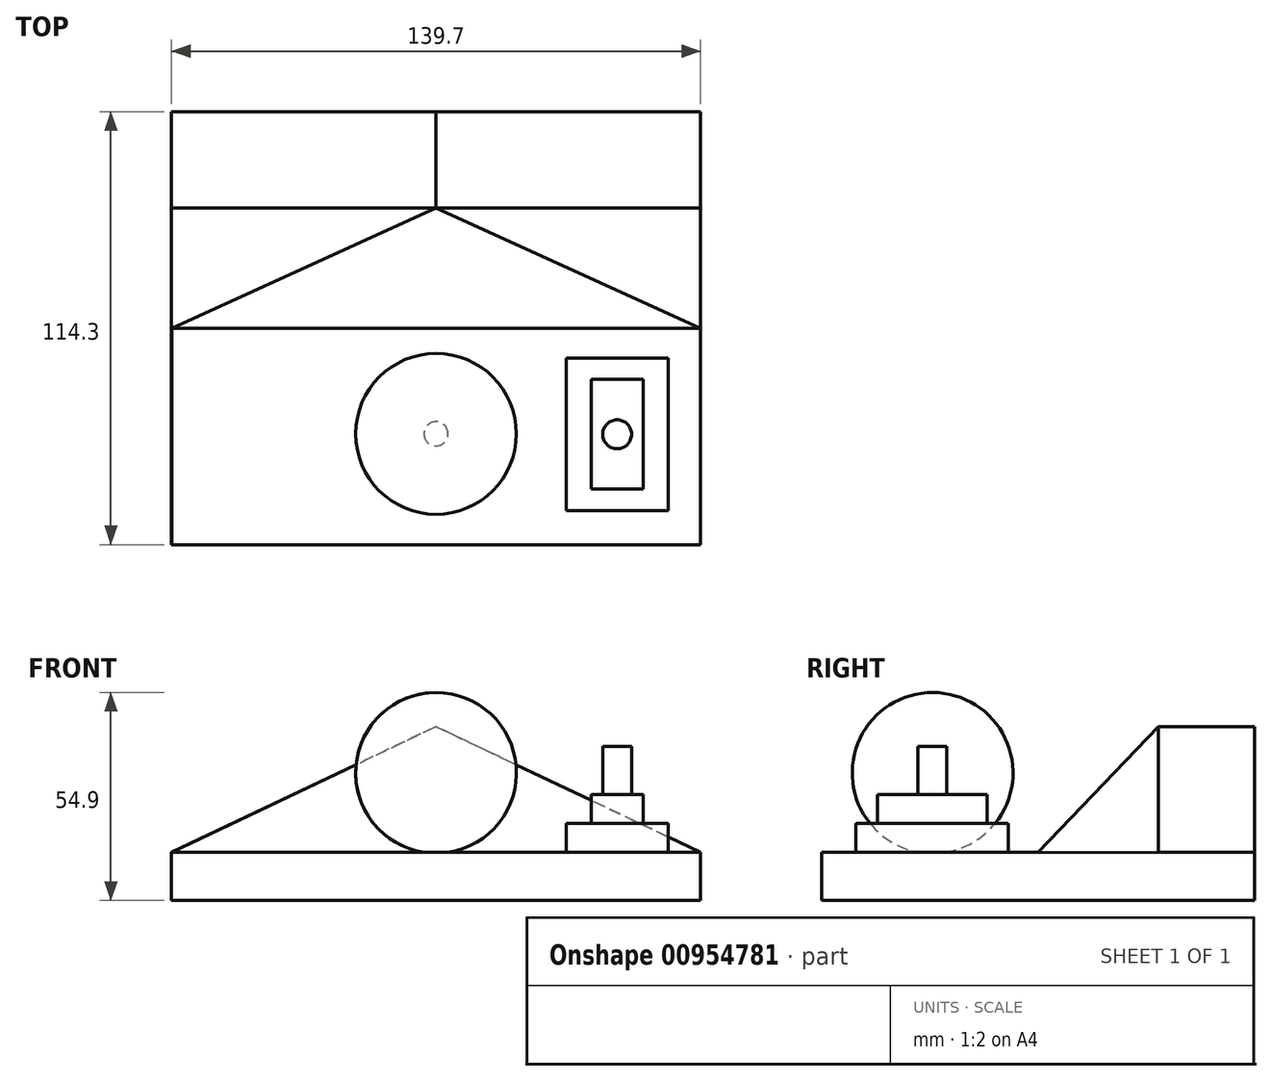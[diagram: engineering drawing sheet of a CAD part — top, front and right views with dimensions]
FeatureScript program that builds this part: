
annotation { "Feature Type Name" : "Feature", "Feature Type Description" : "" }
export const myFeature = defineFeature(function(context is Context, id is Id, definition is map)
    precondition{}
    {
        {
            var Q0;
            Q0=qCreatedBy(makeId("Top.planeOp"),FACE);
            var sketch = newSketch(context, id + "F0", { "sketchPlane" : qUnion([Q0])});
            skLineSegment(sketch, "E0.bottom", {"start": v(69.85, 57.15) * mm, "end": v(-69.85, 57.15) * mm});
            skLineSegment(sketch, "E0.top", {"start": v(69.85, -57.15) * mm, "end": v(-69.85, -57.15) * mm});
            skLineSegment(sketch, "E0.left", {"start": v(69.85, 57.15) * mm, "end": v(69.85, -57.15) * mm});
            skLineSegment(sketch, "E0.right", {"start": v(-69.85, 57.15) * mm, "end": v(-69.85, -57.15) * mm});
            skPoint(sketch, "E0.middle", {"position": v(0, 0) * mm});
            skSolve(sketch);
        }
        {
            var Q0;
            Q0=makeQuery(id+"F0.imprint","IMPRINT",FACE,{"disambiguationData":[TD([[makeQuery(id+"F0.imprint","IMPRINT",EDGE,{"derivedFrom":sQuery(id+"F0.wireOp",EDGE,"E0.bottom")}),1.0]])]});
            extrude(context, id + "F1", {"entities" : qUnion([Q0]), "depth" : 12.7 * mm, "offsetDistance" : 25.4 * mm});
        }
        {
            var Q0;
            Q0=makeQuery(id+"F1.opExtrude","SWEPT_FACE",FACE,{"disambiguationData":[OSD([sQuery(id+"F0.wireOp",EDGE,"E0.bottom")])]});
            var sketch = newSketch(context, id + "F2", { "sketchPlane" : qUnion([Q0])});
            skLineSegment(sketch, "E1", {"start": v(69.85, 12.7) * mm, "end": v(0, 45.9) * mm});
            skLineSegment(sketch, "E2", {"start": v(0, 45.9) * mm, "end": v(-69.85, 12.7) * mm});
            skLineSegment(sketch, "E3", {"start": v(-69.85, 12.7) * mm, "end": v(69.85, 12.7) * mm});
            skSolve(sketch);
        }
        {
            var Q0;
            Q0=makeQuery(id+"F2.imprint","IMPRINT",FACE,{"disambiguationData":[TD([[makeQuery(id+"F2.imprint","IMPRINT",EDGE,{"derivedFrom":sQuery(id+"F2.wireOp",EDGE,"E1")}),1.0]])]});
            extrude(context, id + "F3", {"entities" : qUnion([Q0]), "oppositeDirection" : true, "depth" : 25.4 * mm, "offsetDistance" : 25.4 * mm});
        }
        {
            var Q0;
            Q0=qCreatedBy(makeId("Right.planeOp"),FACE);
            var sketch = newSketch(context, id + "F4", { "sketchPlane" : qUnion([Q0])});
            skLineSegment(sketch, "E4", {"start": v(0, 12.7) * mm, "end": v(31.75, 12.7) * mm});
            skLineSegment(sketch, "E5", {"start": v(31.75, 12.7) * mm, "end": v(31.73, 45.9) * mm});
            skLineSegment(sketch, "E6", {"start": v(31.73, 45.9) * mm, "end": v(0, 12.7) * mm});
            skSolve(sketch);
        }
        {
            var Q0;
            Q0 = qSketchRegion(id + "F4", true);
            extrude(context, id + "F5", {"entities" : qUnion([Q0]), "operationType" : NewBodyOperationType.ADD, "endBound" : BoundingType.SYMMETRIC, "depth" : 139.7 * mm, "offsetDistance" : 25.4 * mm});
        }
        {
            var Q0;
            Q0=makeQuery(id+"F5.opExtrude","SWEPT_FACE",FACE,{"disambiguationData":[OSD([sQuery(id+"F4.wireOp",EDGE,"E5")])]});
            var sketch = newSketch(context, id + "F6", { "sketchPlane" : qUnion([Q0])});
            skLineSegment(sketch, "E7", {"start": v(-69.85, 12.69) * mm, "end": v(0, 45.88) * mm});
            skLineSegment(sketch, "E8", {"start": v(0, 45.88) * mm, "end": v(69.85, 12.69) * mm});
            skLineSegment(sketch, "E9", {"start": v(69.85, 12.69) * mm, "end": v(69.85, 45.88) * mm});
            skLineSegment(sketch, "E10", {"start": v(69.85, 45.88) * mm, "end": v(-69.85, 45.88) * mm});
            skLineSegment(sketch, "E11", {"start": v(-69.85, 45.88) * mm, "end": v(-69.85, 12.69) * mm});
            skSolve(sketch);
        }
        {
            var Q0;
            Q0 = qSketchRegion(id + "F6", true);
            extrude(context, id + "F7", {"entities" : qUnion([Q0]), "operationType" : NewBodyOperationType.REMOVE, "oppositeDirection" : true, "depth" : 152.4 * mm, "offsetDistance" : 25.4 * mm});
        }
        {
            var Q0;
            Q0=qCreatedBy(makeId("Front.planeOp"),FACE);
            cPlane(context, id + "F8", {"entities" : qUnion([Q0]), "cplaneType" : CPlaneType.OFFSET, "offset" : 27.9 * mm, "width" : 152.4 * mm, "height" : 152.4 * mm});
        }
        {
            var Q0;
            Q0=qCreatedBy(id+"F8.planeOp",FACE);
            var sketch = newSketch(context, id + "F9", { "sketchPlane" : qUnion([Q0])});
            skArc(sketch, "E12", {"start": v(0, 12.46) * mm, "mid": v(21.22, 33.68) * mm, "end": v(0, 54.9) * mm});
            skLineSegment(sketch, "E13", {"start": v(0, 54.9) * mm, "end": v(0, 12.46) * mm});
            skSolve(sketch);
        }
        {
            var Q0;
            Q0=qCreatedBy(id+"F8.planeOp",FACE);
            var sketch = newSketch(context, id + "F10", { "sketchPlane" : qUnion([Q0])});
            skLineSegment(sketch, "E14", {"start": v(0, 0) * mm, "end": v(0, 61.95) * mm});
            skSolve(sketch);
        }
        {
            var Q0;
            Q0 = qSketchRegion(id + "F9", true);
            var Q1;
            Q1 = qSketchRegion(id + "F10", true);
            var Q2;
            Q2=sQuery(id+"F10.wireOp",EDGE,"E14");
            var Q3;
            Q3=sQuery(id+"F10.wireOp",EDGE,"E14");
            revolve(context, id + "F11", {"operationType" : NewBodyOperationType.ADD, "surfaceOperationType" : NewSurfaceOperationType.NEW, "entities" : qUnion([Q0, Q1]), "axis" : qUnion([Q2, Q3]), "revolveType" : RevolveType.FULL});
        }
        {
            var Q0;
            {var subQ3=sQuery(id+"F0.wireOp",EDGE,"E0.top");var subQ4=sQuery(id+"F0.wireOp",EDGE,"E0.right");var subQ5=sQuery(id+"F0.wireOp",EDGE,"E0.left");Q0=makeQuery(id+"F5.boolean.opBoolean","SPLIT",FACE,{"disambiguationData":[TD([makeQuery(id+"F1.opExtrude","SWEPT_FACE",FACE,{"disambiguationData":[OSD([subQ3])]})])],"derivedFrom":makeQuery(id+"F1.opExtrude","CAP_FACE",FACE,{"disambiguationData":[OSD([sQuery(id+"F0.wireOp",EDGE,"E0.bottom"),subQ3,subQ5,subQ4])],"isStart":false})});}
            var sketch = newSketch(context, id + "F12", { "sketchPlane" : qUnion([Q0])});
            skLineSegment(sketch, "E15.bottom", {"start": v(34.39, -7.86) * mm, "end": v(61.25, -7.86) * mm});
            skLineSegment(sketch, "E15.top", {"start": v(34.39, -48.15) * mm, "end": v(61.25, -48.15) * mm});
            skLineSegment(sketch, "E15.left", {"start": v(34.39, -7.86) * mm, "end": v(34.39, -48.15) * mm});
            skLineSegment(sketch, "E15.right", {"start": v(61.25, -7.86) * mm, "end": v(61.25, -48.15) * mm});
            skPoint(sketch, "E15.middle", {"position": v(47.82, -28) * mm});
            skSolve(sketch);
        }
        {
            var Q0;
            Q0 = qSketchRegion(id + "F12", true);
            extrude(context, id + "F13", {"entities" : qUnion([Q0]), "operationType" : NewBodyOperationType.ADD, "depth" : 7.62 * mm, "offsetDistance" : 25.4 * mm});
        }
        {
            var Q0;
            Q0=makeQuery(id+"F13.opExtrude","CAP_FACE",FACE,{"disambiguationData":[OSD([sQuery(id+"F12.wireOp",EDGE,"E15.bottom"),sQuery(id+"F12.wireOp",EDGE,"E15.top"),sQuery(id+"F12.wireOp",EDGE,"E15.left"),sQuery(id+"F12.wireOp",EDGE,"E15.right")])],"isStart":false});
            var sketch = newSketch(context, id + "F14", { "sketchPlane" : qUnion([Q0])});
            skLineSegment(sketch, "E16.bottom", {"start": v(54.65, -13.52) * mm, "end": v(40.98, -13.52) * mm});
            skLineSegment(sketch, "E16.top", {"start": v(54.65, -42.5) * mm, "end": v(40.98, -42.5) * mm});
            skLineSegment(sketch, "E16.left", {"start": v(54.65, -13.52) * mm, "end": v(54.65, -42.5) * mm});
            skLineSegment(sketch, "E16.right", {"start": v(40.98, -13.52) * mm, "end": v(40.98, -42.5) * mm});
            skPoint(sketch, "E16.middle", {"position": v(47.82, -28) * mm});
            skPoint(sketch, "E16.middle.positionSnap0", {"position": v(61.25, -28) * mm});
            skPoint(sketch, "E16.middle.positionSnap1", {"position": v(47.82, -7.86) * mm});
            skPoint(sketch, "E16.centerSnap0", {"position": v(61.25, -28) * mm});
            skPoint(sketch, "E16.centerSnap1", {"position": v(47.82, -7.86) * mm});
            skSolve(sketch);
        }
        {
            var Q0;
            Q0 = qSketchRegion(id + "F14", true);
            extrude(context, id + "F15", {"entities" : qUnion([Q0]), "operationType" : NewBodyOperationType.ADD, "depth" : 7.62 * mm, "offsetDistance" : 25.4 * mm});
        }
        {
            var Q0;
            Q0=makeQuery(id+"F15.opExtrude","CAP_FACE",FACE,{"disambiguationData":[OSD([sQuery(id+"F14.wireOp",EDGE,"E16.bottom"),sQuery(id+"F14.wireOp",EDGE,"E16.top"),sQuery(id+"F14.wireOp",EDGE,"E16.left"),sQuery(id+"F14.wireOp",EDGE,"E16.right")])],"isStart":false});
            var sketch = newSketch(context, id + "F16", { "sketchPlane" : qUnion([Q0])});
            skCircle(sketch, "E17", {"center": v(47.82, -28) * mm, "radius": 3.82 * mm});
            skPoint(sketch, "E17.centerSnap0", {"position": v(54.65, -28) * mm});
            skPoint(sketch, "E17.centerSnap1", {"position": v(47.82, -13.52) * mm});
            skSolve(sketch);
        }
        {
            var Q0;
            Q0 = qSketchRegion(id + "F16", true);
            extrude(context, id + "F17", {"entities" : qUnion([Q0]), "operationType" : NewBodyOperationType.ADD, "depth" : 12.7 * mm, "offsetDistance" : 25.4 * mm});
        }
    });
